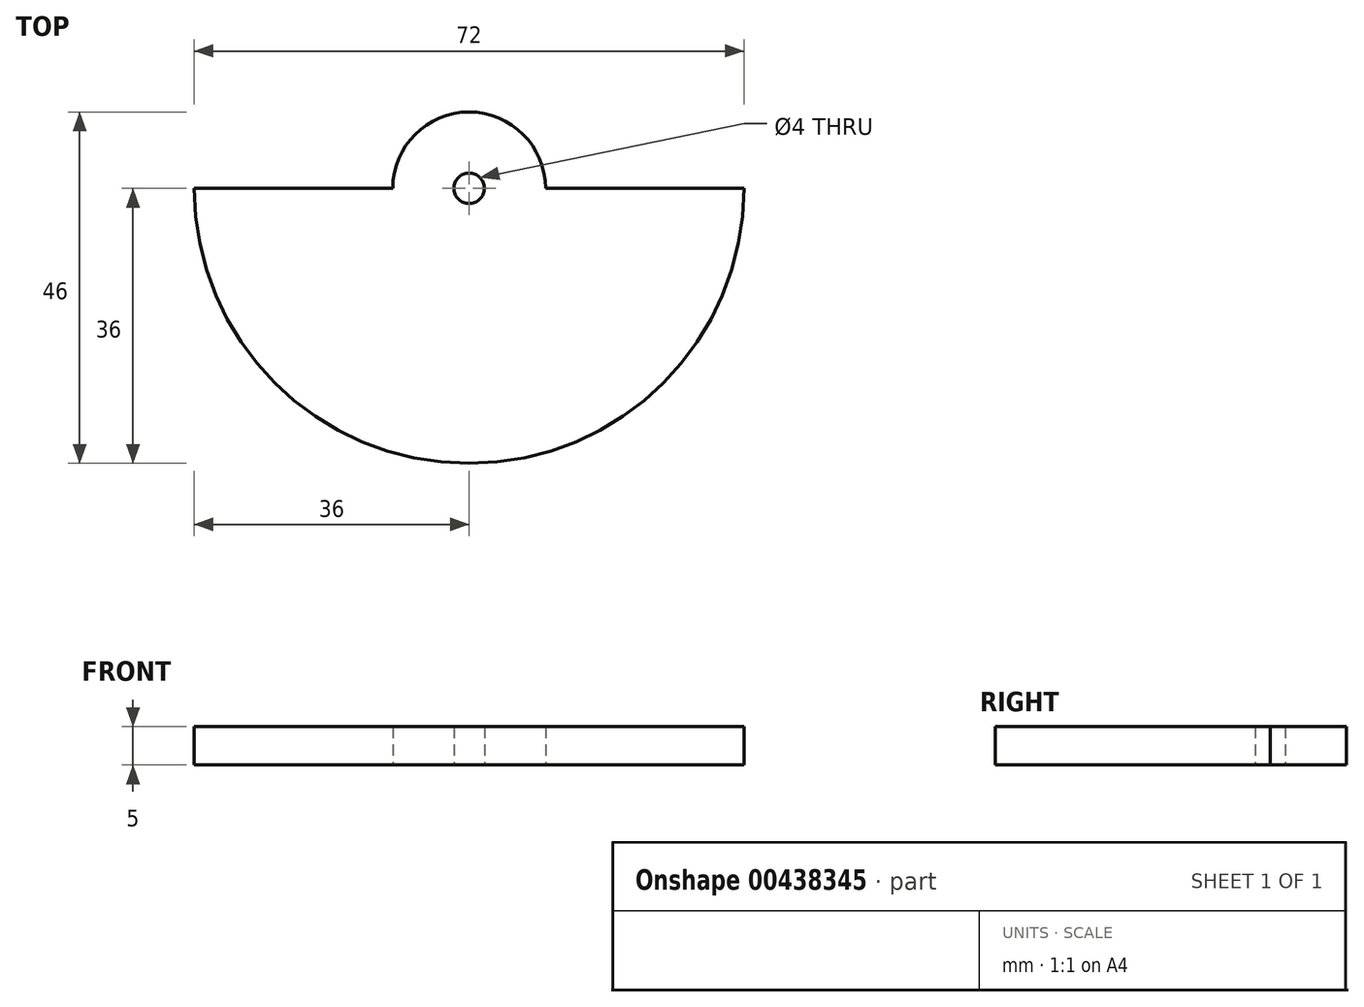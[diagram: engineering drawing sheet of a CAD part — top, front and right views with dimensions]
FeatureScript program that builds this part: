
annotation { "Feature Type Name" : "Feature", "Feature Type Description" : "" }
export const myFeature = defineFeature(function(context is Context, id is Id, definition is map)
    precondition{}
    {
        {
            var Q0;
            Q0=qCreatedBy(makeId("Top.planeOp"),FACE);
            var sketch = newSketch(context, id + "F0", { "sketchPlane" : qUnion([Q0])});
            skCircle(sketch, "E0", {"center": v(0, 0) * mm, "radius": 2 * mm});
            skLineSegment(sketch, "E1", {"start": v(-10, 0) * mm, "end": v(-36, 0) * mm});
            skLineSegment(sketch, "E2", {"start": v(10, 0) * mm, "end": v(36, 0) * mm});
            skArc(sketch, "E3", {"start": v(-36, 0) * mm, "mid": v(0, -36) * mm, "end": v(36, 0) * mm});
            skArc(sketch, "E4", {"start": v(-10, 0) * mm, "mid": v(0, 10) * mm, "end": v(10, 0) * mm});
            skSolve(sketch);
        }
        {
            var Q0;
            Q0=makeQuery(id+"F0.imprint","IMPRINT",FACE,{"disambiguationData":[TD([[makeQuery(id+"F0.imprint","IMPRINT",EDGE,{"derivedFrom":sQuery(id+"F0.wireOp",EDGE,"E0")}),-1.0]])]});
            extrude(context, id + "F1", {"entities" : qUnion([Q0]), "depth" : 5 * mm});
        }
    });
